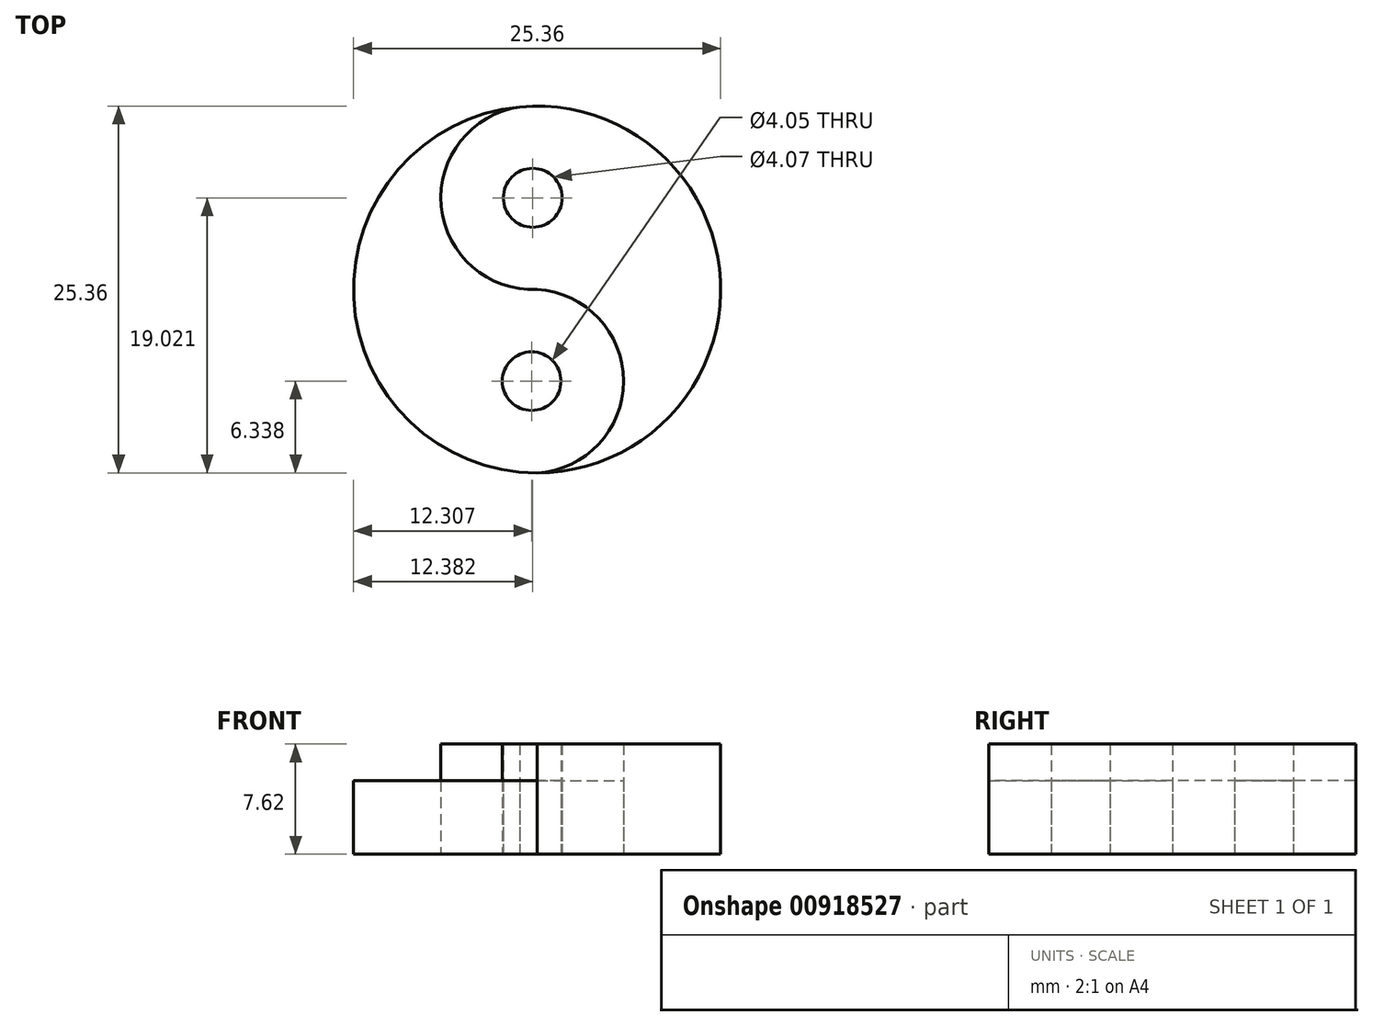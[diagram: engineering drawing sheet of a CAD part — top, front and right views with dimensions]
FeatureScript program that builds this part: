
annotation { "Feature Type Name" : "Feature", "Feature Type Description" : "" }
export const myFeature = defineFeature(function(context is Context, id is Id, definition is map)
    precondition{}
    {
        {
            var Q0;
            Q0=qCreatedBy(makeId("Top.planeOp"),FACE);
            var sketch = newSketch(context, id + "F0", { "sketchPlane" : qUnion([Q0])});
            skCircle(sketch, "E0", {"center": v(0, 0) * mm, "radius": 12.68 * mm});
            skArc(sketch, "E1", {"start": v(0, 12.68) * mm, "mid": v(-6.65, 6.34) * mm, "end": v(0, 0) * mm});
            skArc(sketch, "E2", {"start": v(0, -12.68) * mm, "mid": v(5.98, -6.34) * mm, "end": v(0, 0) * mm});
            skCircle(sketch, "E3", {"center": v(-0.3, 6.34) * mm, "radius": 2.03 * mm});
            skCircle(sketch, "E4", {"center": v(-0.37, -6.34) * mm, "radius": 2.03 * mm});
            skSolve(sketch);
        }
        {
            var Q0;
            {var subQ0=sQuery(id+"F0.wireOp",EDGE,"E2");Q0=makeQuery(id+"F0.imprint","IMPRINT",FACE,{"disambiguationData":[TD([[makeQuery(id+"F0.imprint","IMPRINT",EDGE,{"derivedFrom":subQ0}),-1.0]])]});}
            var Q1;
            Q1=makeQuery(id+"F0.imprint","IMPRINT",FACE,{"disambiguationData":[TD([[makeQuery(id+"F0.imprint","IMPRINT",EDGE,{"derivedFrom":sQuery(id+"F0.wireOp",EDGE,"E4")}),1.0]])]});
            extrude(context, id + "F1", {"entities" : qUnion([Q0, Q1]), "depth" : 7.62 * mm, "offsetDistance" : 25.4 * mm});
        }
        {
            var Q0;
            {var subQ0=sQuery(id+"F0.wireOp",EDGE,"E2");Q0=makeQuery(id+"F0.imprint","IMPRINT",FACE,{"disambiguationData":[TD([[makeQuery(id+"F0.imprint","IMPRINT",EDGE,{"derivedFrom":subQ0}),1.0]])]});}
            var Q1;
            Q1=makeQuery(id+"F0.imprint","IMPRINT",FACE,{"disambiguationData":[TD([[makeQuery(id+"F0.imprint","IMPRINT",EDGE,{"derivedFrom":sQuery(id+"F0.wireOp",EDGE,"E3")}),1.0]])]});
            extrude(context, id + "F2", {"entities" : qUnion([Q0, Q1]), "depth" : 5.08 * mm, "offsetDistance" : 25.4 * mm});
        }
    });
